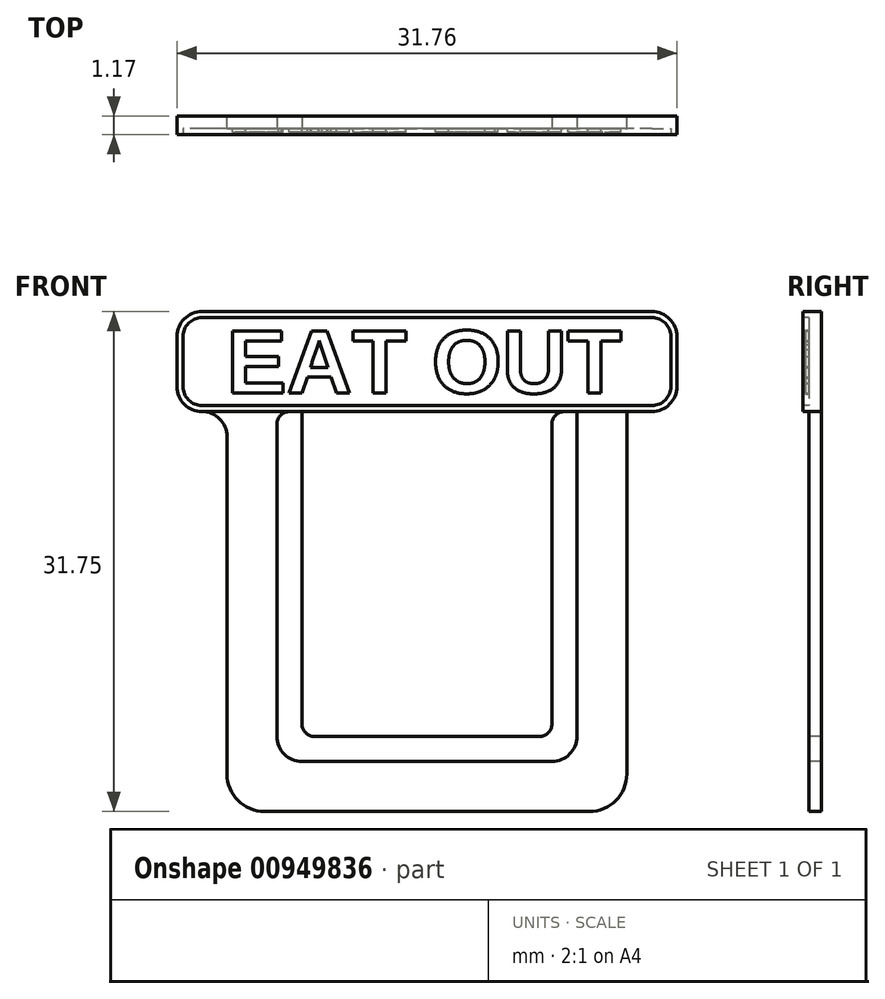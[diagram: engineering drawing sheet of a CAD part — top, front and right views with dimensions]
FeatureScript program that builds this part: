
annotation { "Feature Type Name" : "Feature", "Feature Type Description" : "" }
export const myFeature = defineFeature(function(context is Context, id is Id, definition is map)
    precondition{}
    {
        {
            var Q0;
            Q0=qCreatedBy(makeId("Front.planeOp"),FACE);
            var sketch = newSketch(context, id + "F0", { "sketchPlane" : qUnion([Q0])});
            skLineSegment(sketch, "E0.bottom", {"start": v(12.7, 12.7) * mm, "end": v(-12.7, 12.7) * mm});
            skLineSegment(sketch, "E0.top", {"start": v(12.7, -12.7) * mm, "end": v(-12.7, -12.7) * mm});
            skLineSegment(sketch, "E0.left", {"start": v(12.7, 12.7) * mm, "end": v(12.7, -12.7) * mm});
            skLineSegment(sketch, "E0.right", {"start": v(-12.7, 12.7) * mm, "end": v(-12.7, -12.7) * mm});
            skPoint(sketch, "E0.middle", {"position": v(0, 0) * mm});
            skSolve(sketch);
        }
        {
            var Q0;
            Q0=makeQuery(id+"F0.imprint","IMPRINT",FACE,{"disambiguationData":[TD([[makeQuery(id+"F0.imprint","IMPRINT",EDGE,{"derivedFrom":sQuery(id+"F0.wireOp",EDGE,"E0.bottom")}),1.0]])]});
            extrude(context, id + "F1", {"entities" : qUnion([Q0]), "depth" : 0.8 * mm, "offsetDistance" : 25.4 * mm});
        }
        {
            var Q0;
            Q0=makeQuery(id+"F1.opExtrude","SWEPT_EDGE",EDGE,{"disambiguationData":[OSD([sQuery(id+"F0.wireOp",EDGE,"E0.top"),sQuery(id+"F0.wireOp",EDGE,"E0.left")])]});
            var Q1;
            Q1=makeQuery(id+"F1.opExtrude","SWEPT_EDGE",EDGE,{"disambiguationData":[OSD([sQuery(id+"F0.wireOp",EDGE,"E0.top"),sQuery(id+"F0.wireOp",EDGE,"E0.right")])]});
            fillet(context, id + "F2", {"entities" : qUnion([Q0, Q1]), "radius" : 2.38 * mm, "tangentPropagation" : true, "allowEdgeOverflow" : false});
        }
        {
            var Q0;
            Q0=makeQuery(id+"F1.opExtrude","CAP_FACE",FACE,{"disambiguationData":[OSD([sQuery(id+"F0.wireOp",EDGE,"E0.bottom"),sQuery(id+"F0.wireOp",EDGE,"E0.top"),sQuery(id+"F0.wireOp",EDGE,"E0.left"),sQuery(id+"F0.wireOp",EDGE,"E0.right")])],"isStart":false});
            var sketch = newSketch(context, id + "F3", { "sketchPlane" : qUnion([Q0])});
            skLineSegment(sketch, "E1.bottom", {"start": v(9.52, 12.7) * mm, "end": v(-9.53, 12.7) * mm});
            skLineSegment(sketch, "E1.top", {"start": v(9.53, -9.53) * mm, "end": v(-9.52, -9.53) * mm});
            skLineSegment(sketch, "E1.left", {"start": v(9.52, 12.7) * mm, "end": v(9.53, -9.53) * mm});
            skLineSegment(sketch, "E1.right", {"start": v(-9.53, 12.7) * mm, "end": v(-9.52, -9.53) * mm});
            skPoint(sketch, "E1.middle", {"position": v(0, 0) * mm});
            skSolve(sketch);
        }
        {
            var Q0;
            Q0=makeQuery(id+"F3.imprint","IMPRINT",FACE,{"disambiguationData":[TD([[makeQuery(id+"F3.imprint","IMPRINT",EDGE,{"derivedFrom":sQuery(id+"F3.wireOp",EDGE,"E1.bottom")}),1.0]])]});
            extrude(context, id + "F4", {"entities" : qUnion([Q0]), "operationType" : NewBodyOperationType.REMOVE, "oppositeDirection" : true, "depth" : 4.93 * mm, "offsetDistance" : 25.4 * mm});
        }
        {
            var Q0;
            Q0=makeQuery(id+"F1.opExtrude","CAP_FACE",FACE,{"disambiguationData":[OSD([sQuery(id+"F0.wireOp",EDGE,"E0.bottom"),sQuery(id+"F0.wireOp",EDGE,"E0.top"),sQuery(id+"F0.wireOp",EDGE,"E0.left"),sQuery(id+"F0.wireOp",EDGE,"E0.right")])],"isStart":false});
            var sketch = newSketch(context, id + "F5", { "sketchPlane" : qUnion([Q0])});
            skLineSegment(sketch, "E2.bottom", {"start": v(-15.88, 12.7) * mm, "end": v(15.88, 12.7) * mm});
            skLineSegment(sketch, "E2.top", {"start": v(-15.88, 19.05) * mm, "end": v(15.88, 19.05) * mm});
            skLineSegment(sketch, "E2.left", {"start": v(-15.88, 12.7) * mm, "end": v(-15.88, 19.05) * mm});
            skLineSegment(sketch, "E2.right", {"start": v(15.87, 12.7) * mm, "end": v(15.87, 19.05) * mm});
            skSolve(sketch);
        }
        {
            var Q0;
            Q0=makeQuery(id+"F5.imprint","IMPRINT",FACE,{"disambiguationData":[TD([[makeQuery(id+"F5.imprint","IMPRINT",EDGE,{"derivedFrom":sQuery(id+"F5.wireOp",EDGE,"E2.top")}),-1.0]])]});
            extrude(context, id + "F6", {"entities" : qUnion([Q0]), "operationType" : NewBodyOperationType.ADD, "oppositeDirection" : true, "depth" : 0.8 * mm, "offsetDistance" : 25.4 * mm});
        }
        {
            var Q0;
            Q0=makeQuery(id+"F6.opExtrude","SWEPT_EDGE",EDGE,{"disambiguationData":[OSD([sQuery(id+"F5.wireOp",EDGE,"E2.top"),sQuery(id+"F5.wireOp",EDGE,"E2.left")])]});
            var Q1;
            Q1=makeQuery(id+"F6.opExtrude","SWEPT_EDGE",EDGE,{"disambiguationData":[OSD([sQuery(id+"F5.wireOp",EDGE,"E2.top"),sQuery(id+"F5.wireOp",EDGE,"E2.right")])]});
            var Q2;
            Q2=makeQuery(id+"F6.opExtrude","SWEPT_EDGE",EDGE,{"disambiguationData":[OSD([sQuery(id+"F5.wireOp",EDGE,"E2.bottom"),sQuery(id+"F5.wireOp",EDGE,"E2.right")])]});
            var Q3;
            Q3=makeQuery(id+"F1.opExtrude","SWEPT_EDGE",EDGE,{"disambiguationData":[OSD([sQuery(id+"F0.wireOp",EDGE,"E0.bottom"),sQuery(id+"F0.wireOp",EDGE,"E0.left")])]});
            var Q4;
            Q4=makeQuery(id+"F6.opExtrude","SWEPT_EDGE",EDGE,{"disambiguationData":[OSD([sQuery(id+"F5.wireOp",EDGE,"E2.bottom"),sQuery(id+"F5.wireOp",EDGE,"E2.left")])]});
            var Q5;
            Q5=makeQuery(id+"F1.opExtrude","SWEPT_EDGE",EDGE,{"disambiguationData":[OSD([sQuery(id+"F0.wireOp",EDGE,"E0.bottom"),sQuery(id+"F0.wireOp",EDGE,"E0.right")])]});
            fillet(context, id + "F7", {"entities" : qUnion([Q0, Q1, Q2, Q3, Q4, Q5]), "radius" : 1.59 * mm, "tangentPropagation" : true, "allowEdgeOverflow" : false});
        }
        {
            var Q0;
            Q0=makeQuery(id+"F4.boolean.opBoolean","COPY",EDGE,{"derivedFrom":makeQuery(id+"F4.opExtrude","SWEPT_EDGE",EDGE,{"disambiguationData":[OSD([sQuery(id+"F3.wireOp",EDGE,"E1.top"),sQuery(id+"F3.wireOp",EDGE,"E1.right")])]})});
            var Q1;
            Q1=makeQuery(id+"F4.boolean.opBoolean","COPY",EDGE,{"derivedFrom":makeQuery(id+"F4.opExtrude","SWEPT_EDGE",EDGE,{"disambiguationData":[OSD([sQuery(id+"F3.wireOp",EDGE,"E1.top"),sQuery(id+"F3.wireOp",EDGE,"E1.left")])]})});
            fillet(context, id + "F8", {"entities" : qUnion([Q0, Q1]), "radius" : 1.59 * mm, "tangentPropagation" : true, "allowEdgeOverflow" : false});
        }
        {
            var Q0;
            Q0=makeQuery(id+"F6.boolean.opBoolean","MERGE",FACE,{"derivedFrom":[makeQuery(id+"F1.opExtrude","CAP_FACE",FACE,{"disambiguationData":[OSD([sQuery(id+"F0.wireOp",EDGE,"E0.bottom"),sQuery(id+"F0.wireOp",EDGE,"E0.top"),sQuery(id+"F0.wireOp",EDGE,"E0.left"),sQuery(id+"F0.wireOp",EDGE,"E0.right")])],"isStart":false}),makeQuery(id+"F6.opExtrude","CAP_FACE",FACE,{"disambiguationData":[OSD([sQuery(id+"F5.wireOp",EDGE,"E2.bottom"),sQuery(id+"F5.wireOp",EDGE,"E2.top"),sQuery(id+"F5.wireOp",EDGE,"E2.left"),sQuery(id+"F5.wireOp",EDGE,"E2.right")])],"isStart":true})]});
            var sketch = newSketch(context, id + "F9", { "sketchPlane" : qUnion([Q0])});
            skLineSegment(sketch, "E3.bottom", {"start": v(-7.94, 12.7) * mm, "end": v(7.94, 12.7) * mm});
            skLineSegment(sketch, "E3.top", {"start": v(-7.94, -7.94) * mm, "end": v(7.94, -7.94) * mm});
            skLineSegment(sketch, "E3.left", {"start": v(-7.94, 12.7) * mm, "end": v(-7.94, -7.94) * mm});
            skLineSegment(sketch, "E3.right", {"start": v(7.94, 12.7) * mm, "end": v(7.94, -7.94) * mm});
            skSolve(sketch);
        }
        {
            var Q0;
            Q0=makeQuery(id+"F9.imprint","IMPRINT",FACE,{"disambiguationData":[TD([[makeQuery(id+"F9.imprint","IMPRINT",EDGE,{"derivedFrom":sQuery(id+"F9.wireOp",EDGE,"E3.bottom")}),1.0]])]});
            extrude(context, id + "F10", {"entities" : qUnion([Q0]), "operationType" : NewBodyOperationType.ADD, "oppositeDirection" : true, "depth" : 0.8 * mm, "offsetDistance" : 25.4 * mm});
        }
        {
            var Q0;
            Q0=makeQuery(id+"F10.opExtrude","SWEPT_EDGE",EDGE,{"disambiguationData":[OSD([sQuery(id+"F5.wireOp",EDGE,"E2.bottom"),sQuery(id+"F9.wireOp",EDGE,"E3.bottom"),sQuery(id+"F9.wireOp",EDGE,"E3.left")])]});
            var Q1;
            Q1=makeQuery(id+"F4.boolean.opBoolean","COPY",EDGE,{"derivedFrom":makeQuery(id+"F4.opExtrude","SWEPT_EDGE",EDGE,{"disambiguationData":[OSD([sQuery(id+"F0.wireOp",EDGE,"E0.bottom"),sQuery(id+"F3.wireOp",EDGE,"E1.bottom"),sQuery(id+"F3.wireOp",EDGE,"E1.right")])]})});
            var Q2;
            Q2=makeQuery(id+"F10.opExtrude","SWEPT_EDGE",EDGE,{"disambiguationData":[OSD([sQuery(id+"F5.wireOp",EDGE,"E2.bottom"),sQuery(id+"F9.wireOp",EDGE,"E3.bottom"),sQuery(id+"F9.wireOp",EDGE,"E3.right")])]});
            var Q3;
            Q3=makeQuery(id+"F4.boolean.opBoolean","COPY",EDGE,{"derivedFrom":makeQuery(id+"F4.opExtrude","SWEPT_EDGE",EDGE,{"disambiguationData":[OSD([sQuery(id+"F0.wireOp",EDGE,"E0.bottom"),sQuery(id+"F3.wireOp",EDGE,"E1.bottom"),sQuery(id+"F3.wireOp",EDGE,"E1.left")])]})});
            fillet(context, id + "F11", {"entities" : qUnion([Q0, Q1, Q2, Q3]), "radius" : 0.8 * mm, "tangentPropagation" : true, "allowEdgeOverflow" : false});
        }
        {
            var Q0;
            Q0=makeQuery(id+"F10.opExtrude","SWEPT_EDGE",EDGE,{"disambiguationData":[OSD([sQuery(id+"F9.wireOp",EDGE,"E3.top"),sQuery(id+"F9.wireOp",EDGE,"E3.left")])]});
            var Q1;
            Q1=makeQuery(id+"F10.opExtrude","SWEPT_EDGE",EDGE,{"disambiguationData":[OSD([sQuery(id+"F9.wireOp",EDGE,"E3.top"),sQuery(id+"F9.wireOp",EDGE,"E3.right")])]});
            fillet(context, id + "F12", {"entities" : qUnion([Q0, Q1]), "radius" : 0.8 * mm, "tangentPropagation" : true, "allowEdgeOverflow" : false});
        }
        {
            var Q0;
            Q0=makeQuery(id+"F10.boolean.opBoolean","MERGE",FACE,{"derivedFrom":[makeQuery(id+"F6.boolean.opBoolean","MERGE",FACE,{"derivedFrom":[makeQuery(id+"F1.opExtrude","CAP_FACE",FACE,{"disambiguationData":[OSD([sQuery(id+"F0.wireOp",EDGE,"E0.bottom"),sQuery(id+"F0.wireOp",EDGE,"E0.top"),sQuery(id+"F0.wireOp",EDGE,"E0.left"),sQuery(id+"F0.wireOp",EDGE,"E0.right")])],"isStart":false}),makeQuery(id+"F6.opExtrude","CAP_FACE",FACE,{"disambiguationData":[OSD([sQuery(id+"F5.wireOp",EDGE,"E2.bottom"),sQuery(id+"F5.wireOp",EDGE,"E2.top"),sQuery(id+"F5.wireOp",EDGE,"E2.left"),sQuery(id+"F5.wireOp",EDGE,"E2.right")])],"isStart":true})]}),makeQuery(id+"F10.opExtrude","CAP_FACE",FACE,{"disambiguationData":[OSD([sQuery(id+"F9.wireOp",EDGE,"E3.bottom"),sQuery(id+"F9.wireOp",EDGE,"E3.top"),sQuery(id+"F9.wireOp",EDGE,"E3.left"),sQuery(id+"F9.wireOp",EDGE,"E3.right")])],"isStart":true})]});
            var sketch = newSketch(context, id + "F13", { "sketchPlane" : qUnion([Q0])});
            skArc(sketch, "E4.0", {"start": v(-14.29, 19.05) * mm, "mid": v(-15.41, 18.59) * mm, "end": v(-15.88, 17.46) * mm});
            skLineSegment(sketch, "E5.0", {"start": v(-15.88, 14.29) * mm, "end": v(-15.88, 17.46) * mm});
            skArc(sketch, "E6.0", {"start": v(-15.88, 14.29) * mm, "mid": v(-15.41, 13.16) * mm, "end": v(-14.29, 12.7) * mm});
            skLineSegment(sketch, "E7.0", {"start": v(-14.29, 19.05) * mm, "end": v(14.29, 19.05) * mm});
            skArc(sketch, "E8.0", {"start": v(15.87, 17.46) * mm, "mid": v(15.41, 18.59) * mm, "end": v(14.29, 19.05) * mm});
            skLineSegment(sketch, "E9.0", {"start": v(15.87, 14.29) * mm, "end": v(15.87, 17.46) * mm});
            skArc(sketch, "E10.0", {"start": v(14.29, 12.7) * mm, "mid": v(15.41, 13.16) * mm, "end": v(15.87, 14.29) * mm});
            skLineSegment(sketch, "E11", {"start": v(-14.29, 12.7) * mm, "end": v(14.29, 12.7) * mm});
            skSolve(sketch);
        }
        {
            var Q0;
            Q0=makeQuery(id+"F13.imprint","IMPRINT",FACE,{"disambiguationData":[TD([[makeQuery(id+"F13.imprint","IMPRINT",EDGE,{"derivedFrom":sQuery(id+"F13.wireOp",EDGE,"E4.0")}),1.0]])]});
            extrude(context, id + "F14", {"entities" : qUnion([Q0]), "operationType" : NewBodyOperationType.ADD, "depth" : 0.38 * mm, "offsetDistance" : 25.4 * mm});
        }
        {
            var Q0;
            Q0=makeQuery(id+"F14.opExtrude","CAP_FACE",FACE,{"disambiguationData":[OSD([sQuery(id+"F13.wireOp",EDGE,"E4.0"),sQuery(id+"F13.wireOp",EDGE,"E5.0"),sQuery(id+"F13.wireOp",EDGE,"E6.0"),sQuery(id+"F13.wireOp",EDGE,"E7.0"),sQuery(id+"F13.wireOp",EDGE,"E8.0"),sQuery(id+"F13.wireOp",EDGE,"E9.0"),sQuery(id+"F13.wireOp",EDGE,"E10.0"),sQuery(id+"F13.wireOp",EDGE,"E11")])],"isStart":false});
            var sketch = newSketch(context, id + "F15", { "sketchPlane" : qUnion([Q0])});
            skArc(sketch, "E12.0", {"start": v(-14.29, 19.05) * mm, "mid": v(-15.41, 18.59) * mm, "end": v(-15.88, 17.46) * mm});
            skLineSegment(sketch, "E13.0", {"start": v(-14.29, 19.05) * mm, "end": v(14.29, 19.05) * mm});
            skLineSegment(sketch, "E14.0", {"start": v(-15.88, 14.29) * mm, "end": v(-15.88, 17.46) * mm});
            skArc(sketch, "E15.0", {"start": v(-15.88, 14.29) * mm, "mid": v(-15.41, 13.16) * mm, "end": v(-14.29, 12.7) * mm});
            skLineSegment(sketch, "E16.0", {"start": v(-14.29, 12.7) * mm, "end": v(14.29, 12.7) * mm});
            skArc(sketch, "E17.0", {"start": v(14.29, 12.7) * mm, "mid": v(15.41, 13.16) * mm, "end": v(15.87, 14.29) * mm});
            skArc(sketch, "E18.0", {"start": v(15.87, 17.46) * mm, "mid": v(15.41, 18.59) * mm, "end": v(14.29, 19.05) * mm});
            skArc(sketch, "E19", {"start": v(-14.29, 18.67) * mm, "mid": v(-15.14, 18.32) * mm, "end": v(-15.5, 17.46) * mm});
            skArc(sketch, "E20", {"start": v(-15.5, 14.29) * mm, "mid": v(-15.14, 13.43) * mm, "end": v(-14.29, 13.08) * mm});
            skArc(sketch, "E21", {"start": v(15.5, 17.46) * mm, "mid": v(15.14, 18.32) * mm, "end": v(14.29, 18.67) * mm});
            skArc(sketch, "E22", {"start": v(14.29, 13.08) * mm, "mid": v(15.14, 13.43) * mm, "end": v(15.5, 14.29) * mm});
            skLineSegment(sketch, "E23", {"start": v(-14.29, 19.05) * mm, "end": v(-14.29, 12.7) * mm, "construction": true});
            skLineSegment(sketch, "E24", {"start": v(-15.88, 17.46) * mm, "end": v(15.87, 17.46) * mm, "construction": true});
            skLineSegment(sketch, "E25", {"start": v(14.29, 19.05) * mm, "end": v(14.29, 12.7) * mm, "construction": true});
            skLineSegment(sketch, "E26", {"start": v(15.87, 14.29) * mm, "end": v(-15.88, 14.29) * mm, "construction": true});
            skLineSegment(sketch, "E27", {"start": v(14.29, 18.67) * mm, "end": v(-14.29, 18.67) * mm});
            skLineSegment(sketch, "E28", {"start": v(-15.5, 17.46) * mm, "end": v(-15.5, 14.29) * mm});
            skLineSegment(sketch, "E29", {"start": v(-14.29, 13.08) * mm, "end": v(14.29, 13.08) * mm});
            skLineSegment(sketch, "E30", {"start": v(15.5, 17.46) * mm, "end": v(15.5, 14.29) * mm});
            skSolve(sketch);
        }
        {
            var Q0;
            Q0=makeQuery(id+"F15.imprint","IMPRINT",FACE,{"disambiguationData":[TD([[makeQuery(id+"F15.imprint","IMPRINT",EDGE,{"derivedFrom":sQuery(id+"F15.wireOp",EDGE,"E19")}),1.0]])]});
            var Q1;
            {var subQ0=sQuery(id+"F9.wireOp",EDGE,"E3.right");var subQ1=sQuery(id+"F9.wireOp",EDGE,"E3.top");var subQ3=sQuery(id+"F0.wireOp",EDGE,"E0.bottom");var subQ4=sQuery(id+"F9.wireOp",EDGE,"E3.left");var subQ5=makeQuery(id+"F6.opExtrude","CAP_FACE",FACE,{"disambiguationData":[OSD([sQuery(id+"F5.wireOp",EDGE,"E2.bottom"),sQuery(id+"F5.wireOp",EDGE,"E2.top"),sQuery(id+"F5.wireOp",EDGE,"E2.left"),sQuery(id+"F5.wireOp",EDGE,"E2.right")])],"isStart":true});var subQ6=makeQuery(id+"F1.opExtrude","CAP_FACE",FACE,{"disambiguationData":[OSD([subQ3,sQuery(id+"F0.wireOp",EDGE,"E0.top"),sQuery(id+"F0.wireOp",EDGE,"E0.left"),sQuery(id+"F0.wireOp",EDGE,"E0.right")])],"isStart":false});var subQ7=makeQuery(id+"F10.opExtrude","CAP_FACE",FACE,{"disambiguationData":[OSD([sQuery(id+"F9.wireOp",EDGE,"E3.bottom"),subQ1,subQ4,subQ0])],"isStart":true});Q1=makeQuery(id+"F14.boolean.opBoolean","SPLIT",FACE,{"disambiguationData":[TD([makeQuery(id+"F10.opExtrude","SWEPT_FACE",FACE,{"disambiguationData":[OSD([subQ1])]})])],"derivedFrom":makeQuery(id+"F10.boolean.opBoolean","MERGE",FACE,{"derivedFrom":[makeQuery(id+"F6.boolean.opBoolean","MERGE",FACE,{"derivedFrom":[subQ6,subQ5]}),subQ7]})});}
            extrude(context, id + "F16", {"entities" : qUnion([Q0]), "operationType" : NewBodyOperationType.REMOVE, "endBound" : BoundingType.UP_TO_SURFACE, "oppositeDirection" : true, "depth" : 25.4 * mm, "endBoundEntityFace" : qUnion([Q1]), "offsetDistance" : 25.4 * mm});
        }
        {
            var Q0;
            Q0=qCreatedBy(makeId("Front.planeOp"),FACE);
            var sketch = newSketch(context, id + "F17", { "sketchPlane" : qUnion([Q0])});
            skText(sketch, "E31", { "text": "EAT OUT", "fontName": "Arimo-Bold.ttf"});
            const initialGuessF17  = {"E31": [-0.01272, 0.01388, 1, 0, 0.00412]};
            skSetInitialGuess(sketch, initialGuessF17);
            skSolve(sketch);
        }
        {
            var Q0;
            Q0=qSketchRegion(id+"F17",true);
            extrude(context, id + "F18", {"entities" : qUnion([Q0]), "operationType" : NewBodyOperationType.ADD, "depth" : 1.02 * mm, "offsetDistance" : 25.4 * mm});
        }
    });
